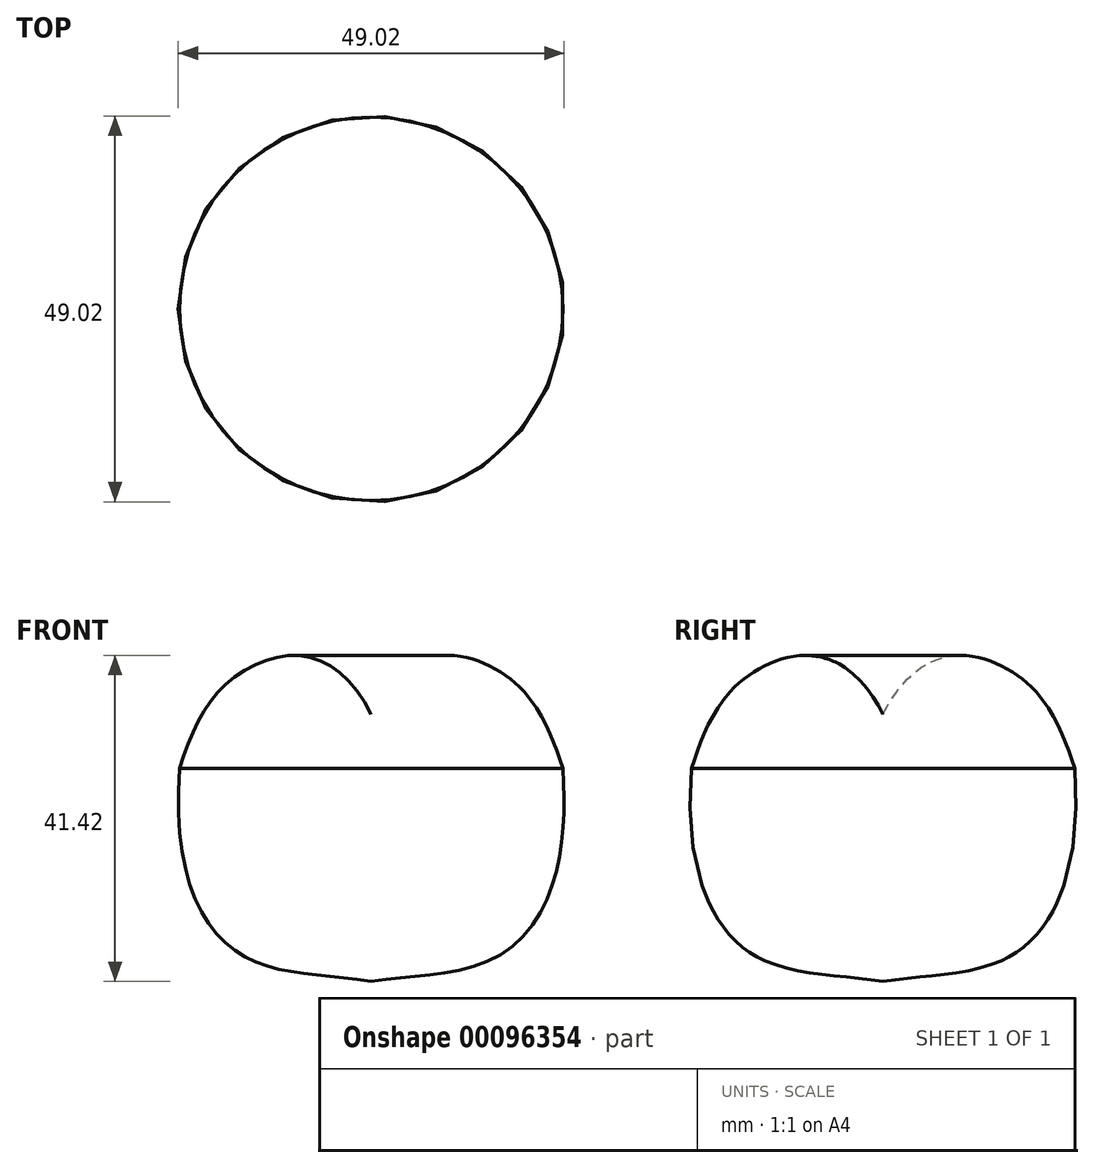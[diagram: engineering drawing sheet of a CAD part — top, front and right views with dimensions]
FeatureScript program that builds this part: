
annotation { "Feature Type Name" : "Feature", "Feature Type Description" : "" }
export const myFeature = defineFeature(function(context is Context, id is Id, definition is map)
    precondition{}
    {
        {
            var Q0;
            Q0=qCreatedBy(makeId("Front.planeOp"),FACE);
            var sketch = newSketch(context, id + "F0", { "sketchPlane" : qUnion([Q0])});
            skFitSpline(sketch, "E0", {"points": [v(-24.35, 27.04) * mm, v(-18.59, 37.64) * mm, v(-8.74, 41.35) * mm, v(0, 33.92) * mm], "startDerivative": vector(12.13, 37.9) * mm, "endDerivative": vector(18.77, -38.57) * mm});
            skLineSegment(sketch, "E1", {"start": v(0, 56.78) * mm, "end": v(0, -34.3) * mm, "construction": true});
            skLineSegment(sketch, "E2", {"start": v(0, 33.92) * mm, "end": v(0, 0) * mm});
            skFitSpline(sketch, "E3", {"points": [v(-24.35, 27.04) * mm, v(-16.54, 3.44) * mm, v(0, 0) * mm], "startDerivative": vector(-5.3, -68.78) * mm, "endDerivative": vector(40.87, -6.36) * mm});
            skSolve(sketch);
        }
        {
            var Q0;
            Q0=makeQuery(id+"F0.imprint","IMPRINT",FACE,{"disambiguationData":[TD([[makeQuery(id+"F0.imprint","IMPRINT",EDGE,{"derivedFrom":sQuery(id+"F0.wireOp",EDGE,"E0")}),-1.0]])]});
            var Q1;
            Q1=sQuery(id+"F0.wireOp",EDGE,"E1");
            revolve(context, id + "F1", {"entities" : qUnion([Q0]), "axis" : qUnion([Q1]), "revolveType" : RevolveType.FULL});
        }
    });
